# Revit family: AD-S162T Loudspeaker Face-Based
name_source: partatom
category: Generic Models
revit_build: Autodesk Revit 2015 (Build: 20150511_0715(x64)
units: mm (PartAtom-declared; Revit-internal decimal feet)

## types (7) — shared parameters
Coverage Horizontal = 150
Coverage Vertical = 30 (WIDE setting), 15 (NARROW setting)
Current Draw = 240
Default Elevation = 4' - 0"
Depth = 5.0in(126mm)
Description = Surface-Mount Loudspeaker
Height = 45.8in(1162mm)
Impedance = 8
Manufacturer = QSC
Manufacturer URL = https://www.qsc.com
Model = AD-S162T
Power Handling = 240
Product Documentation Link = https://www.qsc.com
Product Page URL = https://www.qsc.com
SPL Max = 120 (WIDE setting), 122 (NARROW setting)
Sensitivity = 90 (WIDE setting), 92 (NARROW setting)
Weight = 26lb(11.8kg)
Width = 5.2in(131mm)

## per-type parameters (varying)
| type | Mount Position |
| Mount Position 1 | AD-S162T Loudspeaker : Mount Position 1 |
| Mount Position 2 | AD-S162T Loudspeaker : Mount Position 2 |
| Mount Position 3 | AD-S162T Loudspeaker : Mount Position 3 |
| Mount Position 4 | AD-S162T Loudspeaker : Mount Position 4 |
| Mount Position 5 | AD-S162T Loudspeaker : Mount Position 5 |
| Mount Position 6 | AD-S162T Loudspeaker : Mount Position 6 |
| Mount Position 7 | AD-S162T Loudspeaker : Mount Position 7 |

## geometry (parser evidence)
native form markers: Blend x5, Sweep x14
no freeform markers — native parametric forms only
